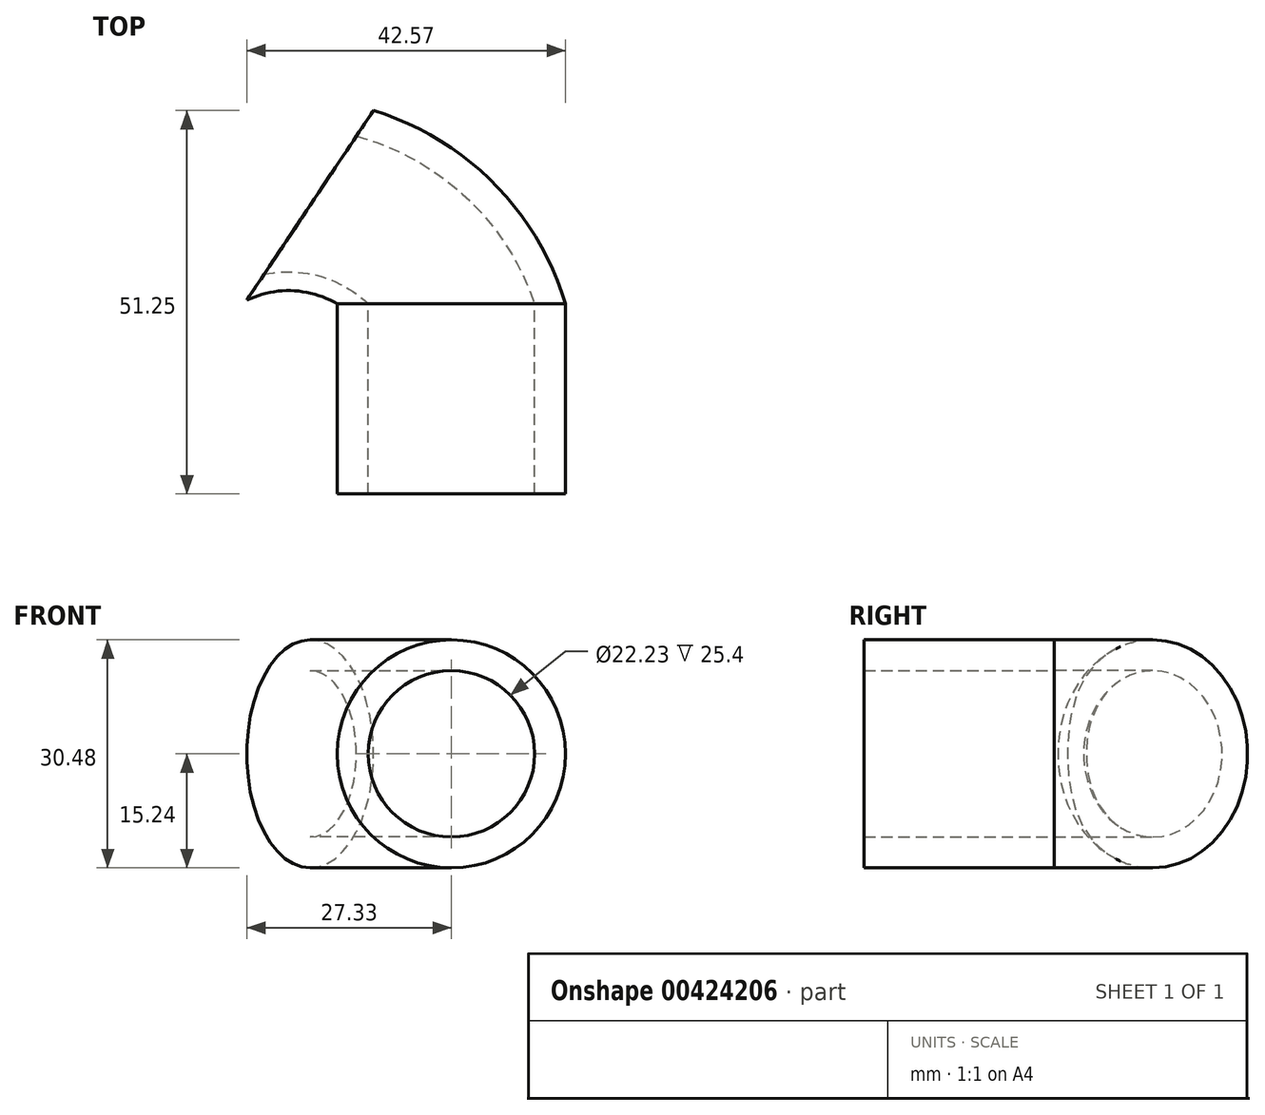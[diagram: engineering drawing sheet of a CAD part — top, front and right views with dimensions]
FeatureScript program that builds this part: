
annotation { "Feature Type Name" : "Feature", "Feature Type Description" : "" }
export const myFeature = defineFeature(function(context is Context, id is Id, definition is map)
    precondition{}
    {
        {
            var Q0;
            Q0=qCreatedBy(makeId("Front.planeOp"),FACE);
            var sketch = newSketch(context, id + "F0", { "sketchPlane" : qUnion([Q0])});
            skPoint(sketch, "E0", {"position": v(20.32, 0) * mm});
            skCircle(sketch, "E1", {"center": v(20.32, 0) * mm, "radius": 15.24 * mm});
            skCircle(sketch, "E2", {"center": v(20.32, 0) * mm, "radius": 11.11 * mm});
            skSolve(sketch);
        }
        {
            var Q0;
            Q0=qSketchRegion(id+"F0",true);
            extrude(context, id + "F1", {"entities" : qUnion([Q0]), "depth" : 25.4 * mm});
        }
        {
            var Q0;
            Q0=qCreatedBy(makeId("Top.planeOp"),FACE);
            var sketch = newSketch(context, id + "F2", { "sketchPlane" : qUnion([Q0])});
            skPoint(sketch, "E3", {"position": v(0, 21.42) * mm});
            skPoint(sketch, "E4", {"position": v(35.02, 0) * mm});
            skPoint(sketch, "E5", {"position": v(9.62, 25.4) * mm});
            skPoint(sketch, "E6", {"position": v(-3.08, 19.05) * mm});
            skArc(sketch, "E7", {"start": v(35.02, 0) * mm, "mid": v(25.5, 15.88) * mm, "end": v(9.62, 25.4) * mm});
            skPoint(sketch, "E8", {"position": v(4.72, 0) * mm});
            skLineSegment(sketch, "E9", {"start": v(4.72, 0) * mm, "end": v(-12.08, 19.05) * mm});
            skSolve(sketch);
        }
        {
            var Q0;
            Q0=makeQuery(id+"F1.opExtrude","CAP_FACE",FACE,{"disambiguationData":[OSD([sQuery(id+"F0.wireOp",EDGE,"E1"),sQuery(id+"F0.wireOp",EDGE,"E2")])],"isStart":true});
            var Q1;
            Q1=sQuery(id+"F2.wireOp",EDGE,"E7");
            sweep(context, id + "F3", {"operationType" : NewBodyOperationType.ADD, "profiles" : qUnion([Q0]), "path" : qUnion([Q1])});
        }
    });
